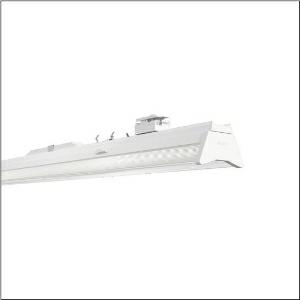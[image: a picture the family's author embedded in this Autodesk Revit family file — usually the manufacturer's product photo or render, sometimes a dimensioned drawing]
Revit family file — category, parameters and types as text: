
# Revit family: licross_r__11_performance_mo_51td16cn49xg_61c3
name_source: partatom
category: Lighting Fixtures
units: mm (PartAtom-declared; Revit-internal decimal feet)

## family parameters
Cut with Voids When Loaded = No
Host = Face
Light Source = No
Part Type = Normal
Room Calculation Point = No
Round Connector Dimension = Use Diameter
Shared = No

## types (1)
- --- (1 x LED, 9190 lm, 49.4 W, 4000K)
    Apparent Load = 49 VA
    CIE Flux Codes = 66 88 96 79 100
    Color Rendering = 80
    Color Temperature = 4000K
    Default Elevation = 1800 mm
    Description = Licross® 11 Performance MO, luminaire insert, of sheet steel, galvanised, coil coated, white, length: 1.500mm, width: 120mm, height: 123mm, LED rated luminous flux: 9.190lm, light colour: 840, control gear: ON/OFF Multilumen, CLOi, with plug, 3-pole, with phase selection, mains connection: 220..240V, AC, 50/60Hz, start of lifetime: 49W, end of service life: 55W, halogen-free wiring, primary light control with lens, of plastic, primary optical cover: cover, of PMMA, light emission: direct/indirect distribution, primary light characteristic: symmetric, protection rating (complete): IP54, insulation class (complete): insulation class I (protective earthing), certification: CE, ENEC, VDE, UKCA, protection symbol: D if used in an environment with non-conductive dust loads with corresponding accessories, impact resistance: IK06, permissible ambient temperature for indoor applications: -35..+40°C, corresponds to IFS (International Featured Standards) requirements for safety and quality in the food industry, reducing of maximum allowable ambient temperature of 5°C with ceiling mounting, LABS conformity tested according to VDMA 24364:2018-05, packaging unit: 1 piece
    Height = 114 mm
    Lamp = 1 x LED
    Lamp Light Flux = 9190 lm
    Lamp Power = 49.4 W
    Lamp count = 1
    Length = 1500 mm
    Luminous efficacy = 186 lm/W
    Manufacturer = Siteco
    ModVariant = No
    Model = 51TD16CN49XG
    Mounting Place = Ceiling
    Mounting Type = Pendant
    Number of Poles = 1
    OnlyDefault = Yes
    Power Factor = 1
    Product Name = Licross® 11 Performance MO
    Product group = luminaire insert
    ProductGroupID = 902
    Protection Class = Protection class I
    Protection Degree = IP 54
    RLX_Detail_Level = 1
    RLX_Emergency_Light_Flux = 0 lm
    RLX_Emergency_Type = 0
    RLX_Emergency_Type_DB = No
    RlxData = <blob elided: 31841 chars, md5=6ec8e11d>
    Socket = socket
    Standby Power = 0 W
    System Light Flux = 9190 lm
    System Power = 49 W
    Type Comments = factory setting: luminous flux: 100 % | (A | C | E) | 113 mA
    Type Image = l_1256138.jpg
    URL = http://relux.com
    VarID = @adj_086070
    Voltage = 0 V
    Weight = 0.00 kg
    Width = 120 mm

## geometry (parser evidence)
native form markers: Blend x4, Sweep x12
no freeform markers — native parametric forms only
